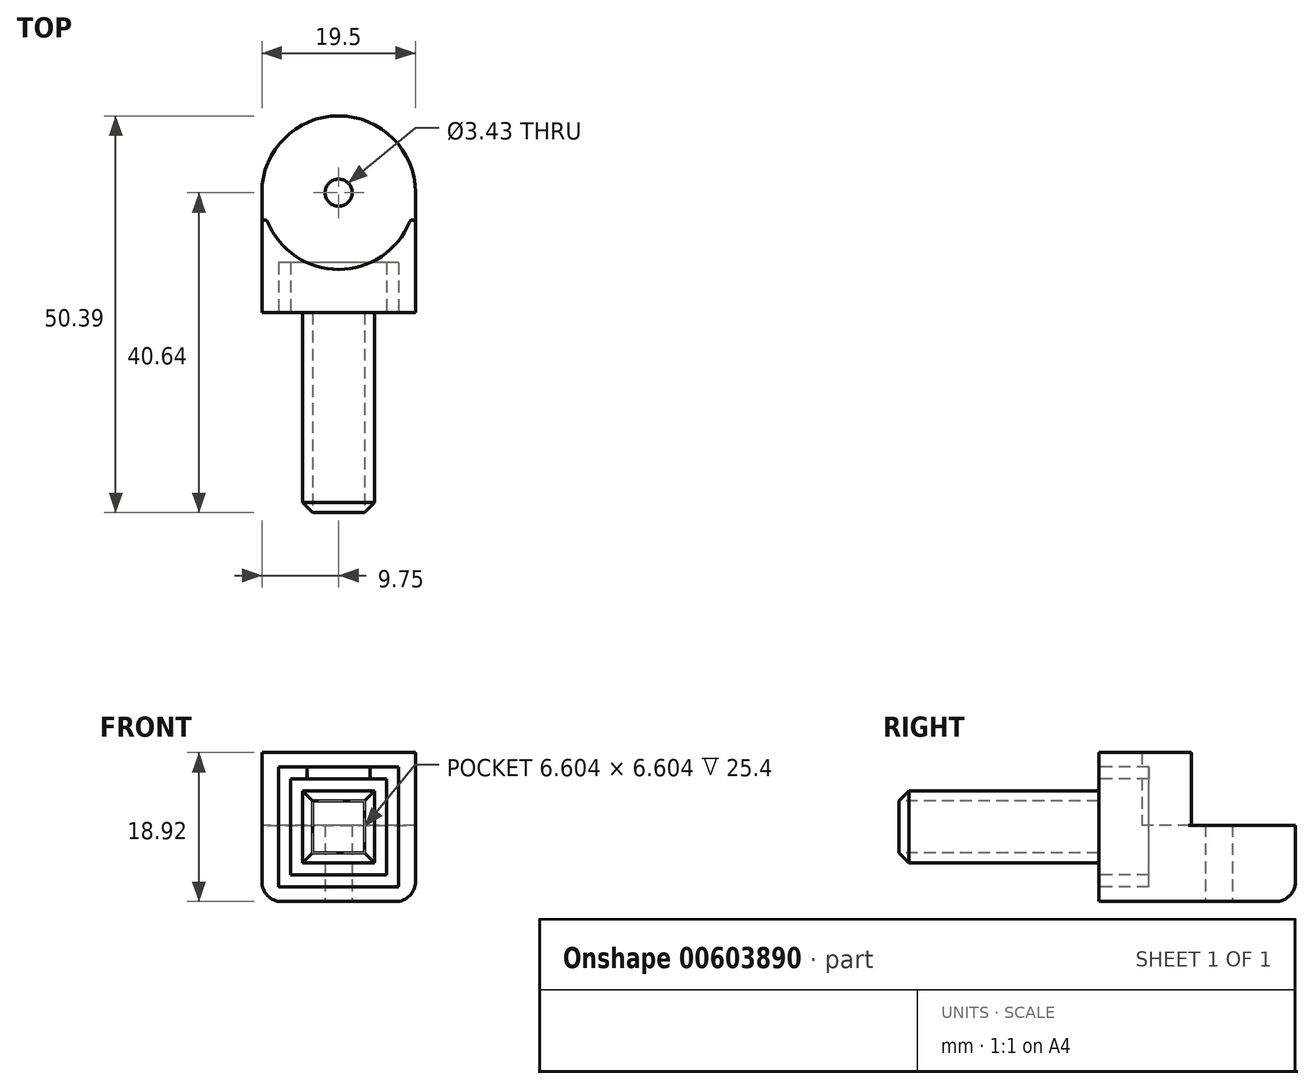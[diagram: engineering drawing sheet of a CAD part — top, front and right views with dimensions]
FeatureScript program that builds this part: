
annotation { "Feature Type Name" : "Feature", "Feature Type Description" : "" }
export const myFeature = defineFeature(function(context is Context, id is Id, definition is map)
    precondition{}
    {
        {
            var Q0;
            Q0=qCreatedBy(makeId("Top.planeOp"),FACE);
            var sketch = newSketch(context, id + "F0", { "sketchPlane" : qUnion([Q0])});
            skCircle(sketch, "E0", {"center": v(0, 0) * mm, "radius": 9.75 * mm});
            skLineSegment(sketch, "E1", {"start": v(9.75, 0) * mm, "end": v(9.75, -15.24) * mm});
            skLineSegment(sketch, "E2", {"start": v(-9.75, 0) * mm, "end": v(-9.75, -15.24) * mm});
            skLineSegment(sketch, "E3", {"start": v(-9.75, -15.24) * mm, "end": v(9.75, -15.24) * mm});
            skPoint(sketch, "E4.endSnap0", {"position": v(0, -15.24) * mm});
            skCircle(sketch, "E5", {"center": v(0, 0) * mm, "radius": 1.71 * mm});
            skSolve(sketch);
        }
        {
            var Q0;
            Q0=makeQuery(id+"F0.imprint","IMPRINT",FACE,{"disambiguationData":[TD([[makeQuery(id+"F0.imprint","IMPRINT",EDGE,{"derivedFrom":sQuery(id+"F0.wireOp",EDGE,"E5")}),-1.0]])]});
            extrude(context, id + "F1", {"entities" : qUnion([Q0]), "depth" : 9.7 * mm, "offsetDistance" : 25.4 * mm});
        }
        {
            var Q0;
            {var subQ0=sQuery(id+"F0.wireOp",EDGE,"E1");Q0=makeQuery(id+"F0.imprint","IMPRINT",FACE,{"disambiguationData":[TD([[makeQuery(id+"F0.imprint","IMPRINT",EDGE,{"derivedFrom":subQ0}),-1.0]])]});}
            extrude(context, id + "F2", {"entities" : qUnion([Q0]), "operationType" : NewBodyOperationType.ADD, "depth" : 18.92 * mm, "offsetDistance" : 25.4 * mm});
        }
        {
            var Q0;
            {var subQ0=sQuery(id+"F0.wireOp",EDGE,"E0");var subQ1=sQuery(id+"F0.wireOp",EDGE,"E2");Q0=makeQuery(id+"F2.boolean.opBoolean","SPLIT",EDGE,{"disambiguationData":[topologyDisambiguationEdgeConnected([makeQuery(id+"F2.opExtrude","SWEPT_FACE",FACE,{"disambiguationData":[OSD([subQ0])]})])],"derivedFrom":makeQuery(id+"F2.opExtrude","SWEPT_EDGE",EDGE,{"disambiguationData":[OSD([subQ0,subQ1])]})});}
            var Q1;
            {var subQ0=sQuery(id+"F0.wireOp",EDGE,"E0");var subQ1=sQuery(id+"F0.wireOp",EDGE,"E1");Q1=makeQuery(id+"F2.boolean.opBoolean","SPLIT",EDGE,{"disambiguationData":[topologyDisambiguationEdgeConnected([makeQuery(id+"F2.opExtrude","SWEPT_FACE",FACE,{"disambiguationData":[OSD([subQ0])]})])],"derivedFrom":makeQuery(id+"F2.opExtrude","SWEPT_EDGE",EDGE,{"disambiguationData":[OSD([subQ0,subQ1])]})});}
            fillet(context, id + "F3", {"entities" : qUnion([Q0, Q1]), "radius" : 0.38 * mm, "tangentPropagation" : true, "allowEdgeOverflow" : false});
        }
        {
            var Q0;
            Q0=makeQuery(id+"F2.opExtrude","SWEPT_FACE",FACE,{"disambiguationData":[OSD([sQuery(id+"F0.wireOp",EDGE,"E3")])]});
            var sketch = newSketch(context, id + "F4", { "sketchPlane" : qUnion([Q0])});
            skLineSegment(sketch, "E6.bottom", {"start": v(4.57, 4.93) * mm, "end": v(-4.57, 4.93) * mm});
            skLineSegment(sketch, "E6.top", {"start": v(4.57, 14.07) * mm, "end": v(-4.57, 14.07) * mm});
            skLineSegment(sketch, "E6.left", {"start": v(4.57, 4.93) * mm, "end": v(4.57, 14.07) * mm});
            skLineSegment(sketch, "E6.right", {"start": v(-4.57, 4.93) * mm, "end": v(-4.57, 14.07) * mm});
            skPoint(sketch, "E6.middle", {"position": v(0, 9.5) * mm});
            skLineSegment(sketch, "E7.bottom", {"start": v(6.1, 3.4) * mm, "end": v(-6.1, 3.4) * mm});
            skLineSegment(sketch, "E7.top", {"start": v(6.1, 15.6) * mm, "end": v(-6.1, 15.6) * mm});
            skLineSegment(sketch, "E7.left", {"start": v(6.1, 3.4) * mm, "end": v(6.1, 15.6) * mm});
            skLineSegment(sketch, "E7.right", {"start": v(-6.1, 3.4) * mm, "end": v(-6.1, 15.6) * mm});
            skLineSegment(sketch, "E8.bottom", {"start": v(7.62, 1.88) * mm, "end": v(-7.62, 1.88) * mm});
            skLineSegment(sketch, "E8.top", {"start": v(7.62, 17.12) * mm, "end": v(-7.62, 17.12) * mm});
            skLineSegment(sketch, "E8.left", {"start": v(7.62, 1.88) * mm, "end": v(7.62, 17.12) * mm});
            skLineSegment(sketch, "E8.right", {"start": v(-7.62, 1.88) * mm, "end": v(-7.62, 17.12) * mm});
            skSolve(sketch);
        }
        {
            var Q0;
            Q0=makeQuery(id+"F4.imprint","IMPRINT",FACE,{"disambiguationData":[TD([[makeQuery(id+"F4.imprint","IMPRINT",EDGE,{"derivedFrom":sQuery(id+"F4.wireOp",EDGE,"E6.bottom")}),-1.0]])]});
            extrude(context, id + "F5", {"entities" : qUnion([Q0]), "operationType" : NewBodyOperationType.ADD, "depth" : 25.4 * mm, "offsetDistance" : 25.4 * mm});
        }
        {
            var Q0;
            Q0=makeQuery(id+"F5.opExtrude","CAP_FACE",FACE,{"disambiguationData":[OSD([sQuery(id+"F4.wireOp",EDGE,"E6.bottom"),sQuery(id+"F4.wireOp",EDGE,"E6.top"),sQuery(id+"F4.wireOp",EDGE,"E6.left"),sQuery(id+"F4.wireOp",EDGE,"E6.right")])],"isStart":false});
            chamfer(context, id + "F6", {"entities" : qUnion([Q0]), "width" : 1.27 * mm, "tangentPropagation" : true});
        }
        {
            var Q0;
            Q0=qCreatedBy(makeId("Top.planeOp"),FACE);
            var sketch = newSketch(context, id + "F7", { "sketchPlane" : qUnion([Q0])});
            skLineSegment(sketch, "E9.bottom", {"start": v(19.43, -5.97) * mm, "end": v(31.37, -5.97) * mm});
            skLineSegment(sketch, "E9.top", {"start": v(19.43, 5.97) * mm, "end": v(31.37, 5.97) * mm});
            skLineSegment(sketch, "E9.left", {"start": v(19.43, -5.97) * mm, "end": v(19.43, 5.97) * mm});
            skLineSegment(sketch, "E9.right", {"start": v(31.37, -5.97) * mm, "end": v(31.37, 5.97) * mm});
            skPoint(sketch, "E9.middle", {"position": v(25.4, 0) * mm});
            skCircle(sketch, "E10", {"center": v(25.4, 0) * mm, "radius": 1.71 * mm});
            skSolve(sketch);
        }
        {
            var Q0;
            Q0=makeQuery(id+"F5.opExtrude","CAP_FACE",FACE,{"disambiguationData":[OSD([sQuery(id+"F4.wireOp",EDGE,"E6.bottom"),sQuery(id+"F4.wireOp",EDGE,"E6.top"),sQuery(id+"F4.wireOp",EDGE,"E6.left"),sQuery(id+"F4.wireOp",EDGE,"E6.right")])],"isStart":false});
            extrude(context, id + "F8", {"entities" : qUnion([Q0]), "operationType" : NewBodyOperationType.REMOVE, "oppositeDirection" : true, "depth" : 25.4 * mm, "offsetDistance" : 25.4 * mm});
        }
        {
            var Q0;
            Q0=makeQuery(id+"F4.imprint","IMPRINT",FACE,{"disambiguationData":[TD([[makeQuery(id+"F4.imprint","IMPRINT",EDGE,{"derivedFrom":sQuery(id+"F4.wireOp",EDGE,"E7.bottom")}),1.0]])]});
            extrude(context, id + "F9", {"entities" : qUnion([Q0]), "operationType" : NewBodyOperationType.REMOVE, "oppositeDirection" : true, "depth" : 6.35 * mm, "offsetDistance" : 25.4 * mm});
        }
        {
            var Q0;
            Q0=makeQuery(id+"F1.opExtrude","CAP_EDGE",EDGE,{"disambiguationData":[OSD([sQuery(id+"F0.wireOp",EDGE,"E0")])],"isStart":true});
            var Q1;
            Q1=makeQuery(id+"F2.opExtrude","CAP_EDGE",EDGE,{"disambiguationData":[OSD([sQuery(id+"F0.wireOp",EDGE,"E1")])],"isStart":true});
            var Q2;
            Q2=makeQuery(id+"F2.opExtrude","CAP_EDGE",EDGE,{"disambiguationData":[OSD([sQuery(id+"F0.wireOp",EDGE,"E2")])],"isStart":true});
            fillet(context, id + "F10", {"entities" : qUnion([Q0, Q1, Q2]), "radius" : 2.54 * mm, "tangentPropagation" : true, "allowEdgeOverflow" : false});
        }
    });
